# Revit family: ERA_Рекуператор тепла_CUPER D125
name_source: partatom
category: Оборудование
units: mm (PartAtom-declared; Revit-internal decimal feet)

## family parameters
Всегда вертикально = Да
Классификация = Нет
На основе рабочей плоскости = Нет
Общий = Нет
При загрузке вырезать с полостями = Нет
Размер круглого соединителя = Использовать диаметр
Тип детали = Нормальный
Точка расчета площади = Нет

## types (1)
- ERA_Рекуператор тепла_CUPER D125
    ADSK_URL документации изделия = https://era.trade
    ADSK_URL страницы изделия = https://era.trade
    ADSK_Версия Revit = 2019
    ADSK_Версия семейства = Ver.1 2025-01
    ADSK_Единица измерения = шт.
    ADSK_Завод-изготовитель = ООО «ЭРА»
    ADSK_Классификация нагрузок = Электродвигатель вентилятора
    ADSK_Код изделия = CUPER 125
    ADSK_Количество = 1
    ADSK_Количество фаз = 1
    ADSK_Количество фаз числовое = 1
    ADSK_Коэффициент мощности = 0.8
    ADSK_Марка = CUPER D125
    ADSK_Материал = ERA_Условный_Белый
    ADSK_Наименование = Рекуператор тепла CUPER D125, 1 скорость
    ADSK_Напряжение = 230 В
    ADSK_Номинальная мощность = 1 Вт
    ADSK_Обозначение = CUPER D125
    ADSK_Полная мощность = 3 В·А
    ADSK_Размер_Высота = 200 мм
    ADSK_Размер_Ширина = 200 мм
    ADSK_Ток = 13 А
    Code1 = 1
    ERA_Гарантия = 2 года
    ERA_Класс защиты = IP24
    ERA_Контакты = 8 (4912) 70-16-76, 8 (4912) 24-16-00
    ERA_Корректированный уровень звуковой мощности = 20
    ERA_Принцип вентиляции = Приточно-вытяжной
    ERA_Страна производитель = Россия
    ERA_Торговая марка = ERA
    ERA_Управление = Автоматическое
    ERA_Цвет = Белый
    ERA_Цвет (декоративный) = White
    LT = ERA_Рекуператор тепла_CUPER D125
    URL = https://era.trade
    r1 = 406 мм
    r2 = 412 мм
    Изготовитель = ООО «ЭРА»
    Производитель_Контакты_Телефон = 8 (4912) 70-16-76, 8 (4912) 24-16-00
